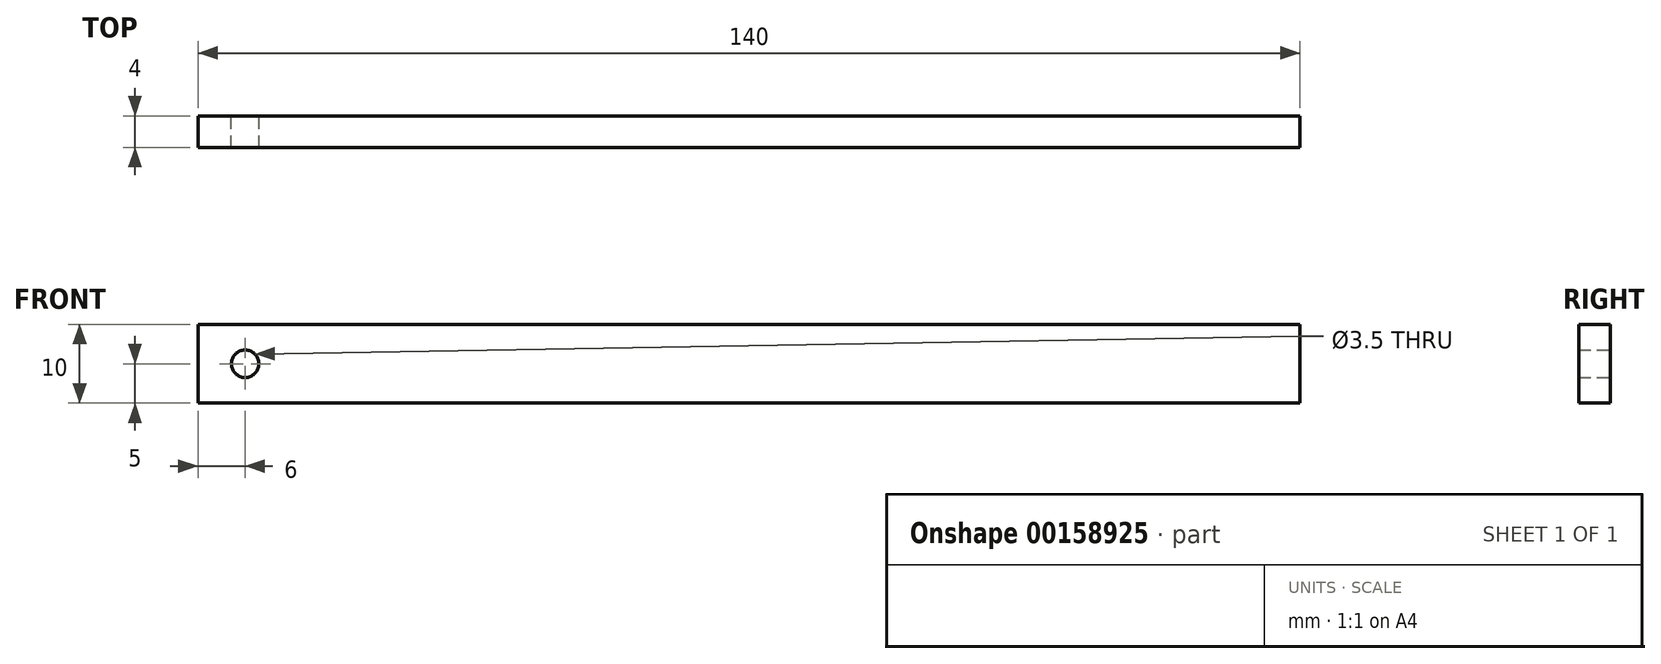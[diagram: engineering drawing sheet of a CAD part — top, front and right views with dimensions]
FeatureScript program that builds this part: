
annotation { "Feature Type Name" : "Feature", "Feature Type Description" : "" }
export const myFeature = defineFeature(function(context is Context, id is Id, definition is map)
    precondition{}
    {
        {
            var Q0;
            Q0=qCreatedBy(makeId("Front.planeOp"),FACE);
            var sketch = newSketch(context, id + "F0", { "sketchPlane" : qUnion([Q0])});
            skLineSegment(sketch, "E0.bottom", {"start": v(-70, 5) * mm, "end": v(70, 5) * mm});
            skLineSegment(sketch, "E0.top", {"start": v(-70, -5) * mm, "end": v(70, -5) * mm});
            skLineSegment(sketch, "E0.left", {"start": v(-70, 5) * mm, "end": v(-70, -5) * mm});
            skLineSegment(sketch, "E0.right", {"start": v(70, 5) * mm, "end": v(70, -5) * mm});
            skPoint(sketch, "E0.middle", {"position": v(0, 0) * mm});
            skSolve(sketch);
        }
        {
            var Q0;
            Q0 = qSketchRegion(id + "F0", true);
            extrude(context, id + "F1", {"entities" : qUnion([Q0]), "depth" : 4 * mm});
        }
        {
            var Q0;
            Q0=qCreatedBy(makeId("Front.planeOp"),FACE);
            var sketch = newSketch(context, id + "F2", { "sketchPlane" : qUnion([Q0])});
            skCircle(sketch, "E1", {"center": v(-64, 0) * mm, "radius": 1.75 * mm});
            skSolve(sketch);
        }
        {
            var Q0;
            Q0=makeQuery(id+"F2.imprint","IMPRINT",FACE,{"disambiguationData":[TD([[makeQuery(id+"F2.imprint","IMPRINT",EDGE,{"derivedFrom":sQuery(id+"F2.wireOp",EDGE,"E1")}),1.0]])]});
            var Q1;
            Q1=sQuery(id+"F2.wireOp",EDGE,"E1");
            extrude(context, id + "F3", {"entities" : qUnion([Q0]), "operationType" : NewBodyOperationType.REMOVE, "surfaceEntities" : qUnion([Q1]), "endBound" : BoundingType.THROUGH_ALL, "depth" : 25 * mm});
        }
    });
